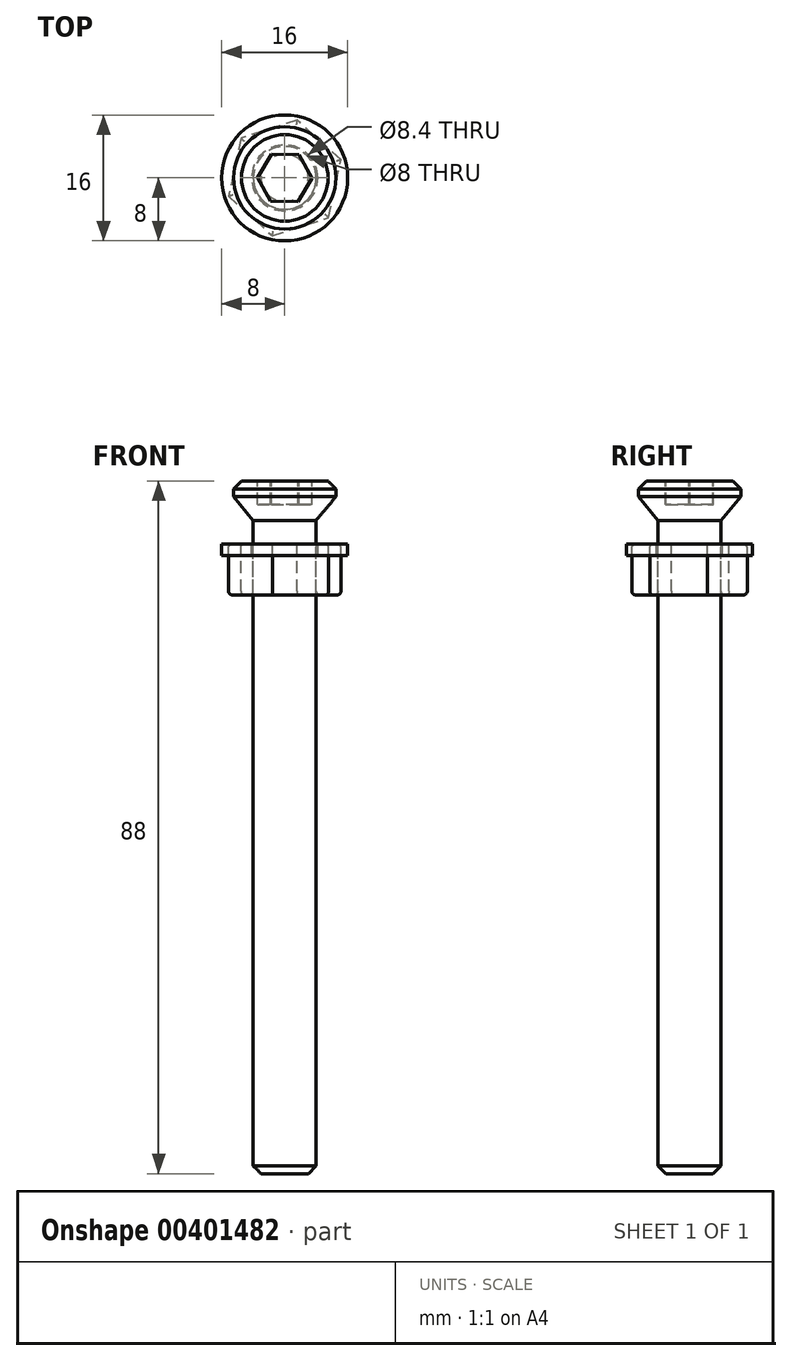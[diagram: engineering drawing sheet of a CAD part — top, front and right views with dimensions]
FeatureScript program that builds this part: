
annotation { "Feature Type Name" : "Feature", "Feature Type Description" : "" }
export const myFeature = defineFeature(function(context is Context, id is Id, definition is map)
    precondition{}
    {
        {
            var Q0;
            Q0=qCreatedBy(makeId("Top.planeOp"),FACE);
            var sketch = newSketch(context, id + "F0", { "sketchPlane" : qUnion([Q0])});
            skCircle(sketch, "E0", {"center": v(0, 0) * mm, "radius": 6.5 * mm});
            skSolve(sketch);
        }
        {
            var Q0;
            Q0=qSketchRegion(id+"F0",true);
            extrude(context, id + "F1", {"entities" : qUnion([Q0]), "depth" : 8 * mm});
        }
        {
            var Q0;
            Q0=makeQuery(id+"F1.opExtrude","CAP_FACE",FACE,{"disambiguationData":[OSD([sQuery(id+"F0.wireOp",EDGE,"E0")])],"isStart":true});
            var sketch = newSketch(context, id + "F2", { "sketchPlane" : qUnion([Q0])});
            skCircle(sketch, "E1", {"center": v(0, 0) * mm, "radius": 4 * mm});
            skSolve(sketch);
        }
        {
            var Q0;
            Q0=qSketchRegion(id+"F2",true);
            extrude(context, id + "F3", {"entities" : qUnion([Q0]), "operationType" : NewBodyOperationType.ADD, "depth" : 80 * mm});
        }
        {
            var Q0;
            Q0=makeQuery(id+"F1.opExtrude","CAP_FACE",FACE,{"disambiguationData":[OSD([sQuery(id+"F0.wireOp",EDGE,"E0")])],"isStart":false});
            var sketch = newSketch(context, id + "F4", { "sketchPlane" : qUnion([Q0])});
            skCircle(sketch, "E2.cCircle", {"center": v(0, 0) * mm, "radius": 3 * mm, "construction": true});
            skLineSegment(sketch, "E2.0", {"start": v(-3.46, 0.06) * mm, "end": v(-1.68, 3.03) * mm});
            skLineSegment(sketch, "E2.1", {"start": v(-1.68, 3.03) * mm, "end": v(1.78, 2.97) * mm});
            skLineSegment(sketch, "E2.2", {"start": v(1.78, 2.97) * mm, "end": v(3.46, -0.06) * mm});
            skLineSegment(sketch, "E2.3", {"start": v(3.46, -0.06) * mm, "end": v(1.68, -3.03) * mm});
            skLineSegment(sketch, "E2.4", {"start": v(1.68, -3.03) * mm, "end": v(-1.78, -2.97) * mm});
            skLineSegment(sketch, "E2.5", {"start": v(-1.78, -2.97) * mm, "end": v(-3.46, 0.06) * mm});
            skPoint(sketch, "E2.0.midPoint", {"position": v(-2.57, 1.55) * mm});
            skSolve(sketch);
        }
        {
            var Q0;
            Q0=qSketchRegion(id+"F4",true);
            extrude(context, id + "F5", {"entities" : qUnion([Q0]), "operationType" : NewBodyOperationType.REMOVE, "oppositeDirection" : true, "depth" : 3 * mm});
        }
        {
            var Q0;
            Q0=makeQuery(id+"F3.opExtrude","CAP_EDGE",EDGE,{"disambiguationData":[OSD([sQuery(id+"F2.wireOp",EDGE,"E1")])],"isStart":false});
            var Q1;
            Q1=makeQuery(id+"F1.opExtrude","CAP_EDGE",EDGE,{"disambiguationData":[OSD([sQuery(id+"F0.wireOp",EDGE,"E0")])],"isStart":false});
            chamfer(context, id + "F6", {"entities" : qUnion([Q0, Q1]), "width" : 1 * mm, "tangentPropagation" : true});
        }
        {
            var Q0;
            Q0=makeQuery(id+"F1.opExtrude","CAP_FACE",FACE,{"disambiguationData":[OSD([sQuery(id+"F0.wireOp",EDGE,"E0")])],"isStart":true});
            var sketch = newSketch(context, id + "F7", { "sketchPlane" : qUnion([Q0])});
            skCircle(sketch, "E3.cCircle", {"center": v(0, 0) * mm, "radius": 6.5 * mm, "construction": true});
            skLineSegment(sketch, "E3.0", {"start": v(7.14, -2.3) * mm, "end": v(1.58, -7.34) * mm});
            skLineSegment(sketch, "E3.1", {"start": v(1.58, -7.34) * mm, "end": v(-5.57, -5.03) * mm});
            skLineSegment(sketch, "E3.2", {"start": v(-5.57, -5.03) * mm, "end": v(-7.14, 2.3) * mm});
            skLineSegment(sketch, "E3.3", {"start": v(-7.14, 2.3) * mm, "end": v(-1.58, 7.34) * mm});
            skLineSegment(sketch, "E3.4", {"start": v(-1.58, 7.34) * mm, "end": v(5.57, 5.03) * mm});
            skLineSegment(sketch, "E3.5", {"start": v(5.57, 5.03) * mm, "end": v(7.14, -2.3) * mm});
            skPoint(sketch, "E3.0.midPoint", {"position": v(4.36, -4.82) * mm});
            skCircle(sketch, "E4", {"center": v(0, 0) * mm, "radius": 4 * mm});
            skSolve(sketch);
        }
        {
            var Q0;
            Q0=qSketchRegion(id+"F7",true);
            extrude(context, id + "F8", {"entities" : qUnion([Q0]), "depth" : 6.5 * mm});
        }
        {
            var Q0;
            Q0=makeQuery(id+"F8.opExtrude","CAP_FACE",FACE,{"disambiguationData":[OSD([sQuery(id+"F7.wireOp",EDGE,"E3.0"),sQuery(id+"F7.wireOp",EDGE,"E3.1"),sQuery(id+"F7.wireOp",EDGE,"E3.2"),sQuery(id+"F7.wireOp",EDGE,"E3.3"),sQuery(id+"F7.wireOp",EDGE,"E3.4"),sQuery(id+"F7.wireOp",EDGE,"E3.5")])],"isStart":false});
            var Q1;
            Q1=makeQuery(id+"F8.opExtrude","CAP_FACE",FACE,{"disambiguationData":[OSD([sQuery(id+"F7.wireOp",EDGE,"E3.0"),sQuery(id+"F7.wireOp",EDGE,"E3.1"),sQuery(id+"F7.wireOp",EDGE,"E3.2"),sQuery(id+"F7.wireOp",EDGE,"E3.3"),sQuery(id+"F7.wireOp",EDGE,"E3.4"),sQuery(id+"F7.wireOp",EDGE,"E3.5")])],"isStart":true});
            fillet(context, id + "F9", {"entities" : qUnion([Q0, Q1]), "radius" : .5 * mm, "tangentPropagation" : true, "allowEdgeOverflow" : false});
        }
        {
            var Q0;
            Q0=makeQuery(id+"F1.opExtrude","CAP_FACE",FACE,{"disambiguationData":[OSD([sQuery(id+"F0.wireOp",EDGE,"E0")])],"isStart":true});
            var sketch = newSketch(context, id + "F10", { "sketchPlane" : qUnion([Q0])});
            skCircle(sketch, "E5", {"center": v(0, 0) * mm, "radius": 8 * mm});
            skCircle(sketch, "E6", {"center": v(0, 0) * mm, "radius": 4.2 * mm});
            skSolve(sketch);
        }
        {
            var Q0;
            Q0=qSketchRegion(id+"F10",true);
            extrude(context, id + "F11", {"entities" : qUnion([Q0]), "depth" : 1.5 * mm});
        }
        {
            var Q0;
            Q0=makeQuery(id+"F1.opExtrude","CAP_EDGE",EDGE,{"disambiguationData":[OSD([sQuery(id+"F0.wireOp",EDGE,"E0")])],"isStart":true});
            chamfer(context, id + "F12", {"entities" : qUnion([Q0]), "chamferType" : ChamferType.TWO_OFFSETS, "width1" : 6 * mm, "oppositeDirection" : false, "width2" : 5 * mm, "tangentPropagation" : true});
        }
    });
